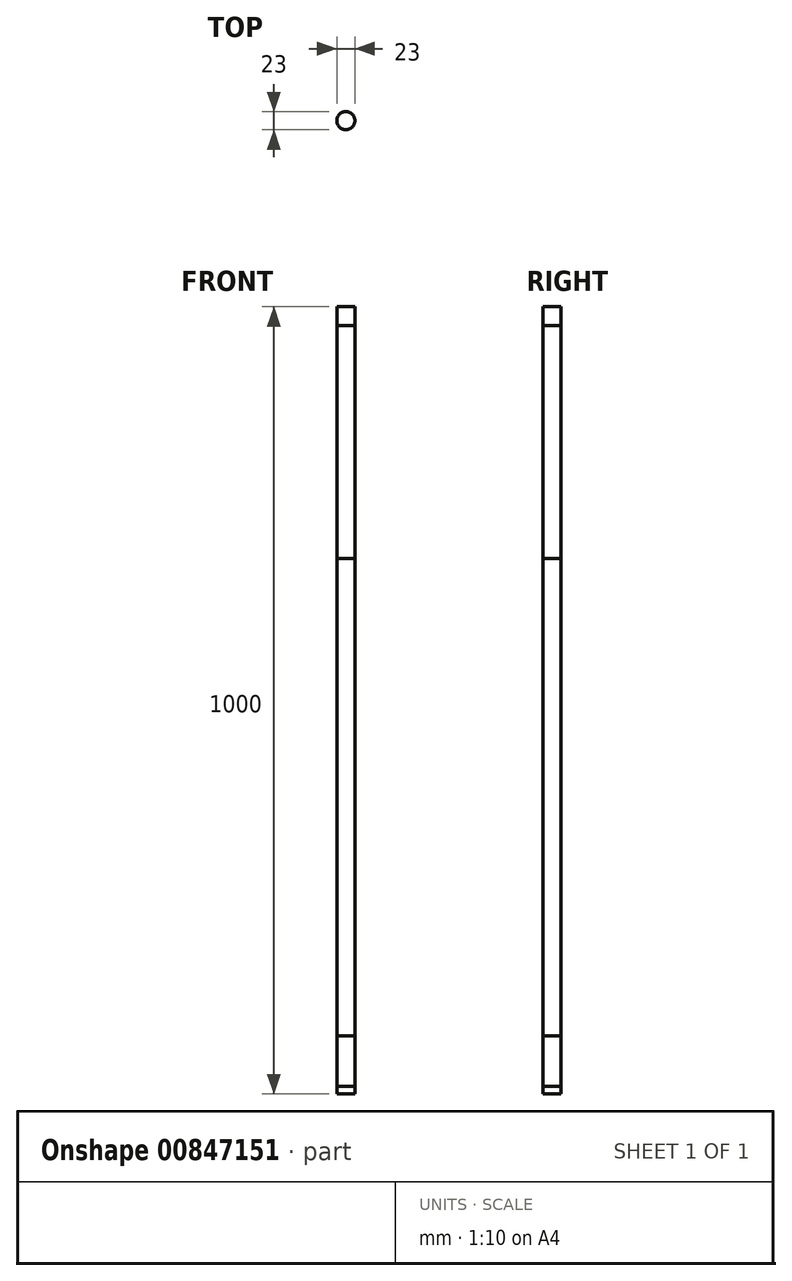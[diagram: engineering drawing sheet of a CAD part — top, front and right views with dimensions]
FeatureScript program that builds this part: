
annotation { "Feature Type Name" : "Feature", "Feature Type Description" : "" }
export const myFeature = defineFeature(function(context is Context, id is Id, definition is map)
    precondition{}
    {
        {
            var Q0;
            Q0=qCreatedBy(makeId("Top.planeOp"),FACE);
            var sketch = newSketch(context, id + "F0", { "sketchPlane" : qUnion([Q0])});
            skCircle(sketch, "E0", {"center": v(0, 0) * mm, "radius": 11.5 * mm});
            skSolve(sketch);
        }
        {
            var Q0;
            Q0=makeQuery(id+"F0.imprint","IMPRINT",FACE,{"disambiguationData":[TD([[makeQuery(id+"F0.imprint","IMPRINT",EDGE,{"derivedFrom":sQuery(id+"F0.wireOp",EDGE,"E0")}),1.0]])]});
            extrude(context, id + "F1", {"entities" : qUnion([Q0]), "depth" : 10 * mm, "offsetDistance" : 25 * mm});
        }
        {
            var Q0;
            Q0=makeQuery(id+"F1.opExtrude","CAP_FACE",FACE,{"disambiguationData":[OSD([sQuery(id+"F0.wireOp",EDGE,"E0")])],"isStart":false});
            cPlane(context, id + "F2", {"entities" : qUnion([Q0]), "cplaneType" : CPlaneType.OFFSET, "offset" : 0 * mm, "width" : 150 * mm, "height" : 150 * mm});
        }
        {
            var Q0;
            Q0=qCreatedBy(id+"F2.planeOp",FACE);
            var sketch = newSketch(context, id + "F3", { "sketchPlane" : qUnion([Q0])});
            skCircle(sketch, "E1", {"center": v(0, 0) * mm, "radius": 11.5 * mm});
            skSolve(sketch);
        }
        {
            var Q0;
            Q0 = qSketchRegion(id + "F3", true);
            extrude(context, id + "F4", {"entities" : qUnion([Q0]), "depth" : 64 * mm, "offsetDistance" : 25 * mm});
        }
        {
            var Q0;
            Q0=makeQuery(id+"F4.opExtrude","CAP_FACE",FACE,{"disambiguationData":[OSD([sQuery(id+"F3.wireOp",EDGE,"E1")])],"isStart":false});
            cPlane(context, id + "F5", {"entities" : qUnion([Q0]), "cplaneType" : CPlaneType.OFFSET, "offset" : 0 * mm, "width" : 150 * mm, "height" : 150 * mm});
        }
        {
            var Q0;
            Q0=qCreatedBy(id+"F5.planeOp",FACE);
            var sketch = newSketch(context, id + "F6", { "sketchPlane" : qUnion([Q0])});
            skCircle(sketch, "E2", {"center": v(0, 0) * mm, "radius": 11.5 * mm});
            skSolve(sketch);
        }
        {
            var Q0;
            Q0 = qSketchRegion(id + "F6", true);
            extrude(context, id + "F7", {"entities" : qUnion([Q0]), "depth" : 606 * mm, "offsetDistance" : 25 * mm});
        }
        {
            var Q0;
            Q0=makeQuery(id+"F7.opExtrude","CAP_FACE",FACE,{"disambiguationData":[OSD([sQuery(id+"F6.wireOp",EDGE,"E2")])],"isStart":false});
            cPlane(context, id + "F8", {"entities" : qUnion([Q0]), "cplaneType" : CPlaneType.OFFSET, "offset" : 0 * mm, "width" : 150 * mm, "height" : 150 * mm});
        }
        {
            var Q0;
            Q0=qCreatedBy(id+"F8.planeOp",FACE);
            var sketch = newSketch(context, id + "F9", { "sketchPlane" : qUnion([Q0])});
            skCircle(sketch, "E3", {"center": v(0, 0) * mm, "radius": 11.5 * mm});
            skSolve(sketch);
        }
        {
            var Q0;
            Q0 = qSketchRegion(id + "F9", true);
            extrude(context, id + "F10", {"entities" : qUnion([Q0]), "depth" : 296 * mm, "offsetDistance" : 25 * mm});
        }
        {
            var Q0;
            Q0=makeQuery(id+"F10.opExtrude","CAP_FACE",FACE,{"disambiguationData":[OSD([sQuery(id+"F9.wireOp",EDGE,"E3")])],"isStart":false});
            cPlane(context, id + "F11", {"entities" : qUnion([Q0]), "cplaneType" : CPlaneType.OFFSET, "offset" : 0 * mm, "width" : 150 * mm, "height" : 150 * mm});
        }
        {
            var Q0;
            Q0=qCreatedBy(id+"F11.planeOp",FACE);
            var sketch = newSketch(context, id + "F12", { "sketchPlane" : qUnion([Q0])});
            skCircle(sketch, "E4", {"center": v(0, 0) * mm, "radius": 11.5 * mm});
            skSolve(sketch);
        }
        {
            var Q0;
            Q0 = qSketchRegion(id + "F12", true);
            extrude(context, id + "F13", {"entities" : qUnion([Q0]), "depth" : 24 * mm, "offsetDistance" : 25 * mm});
        }
    });
